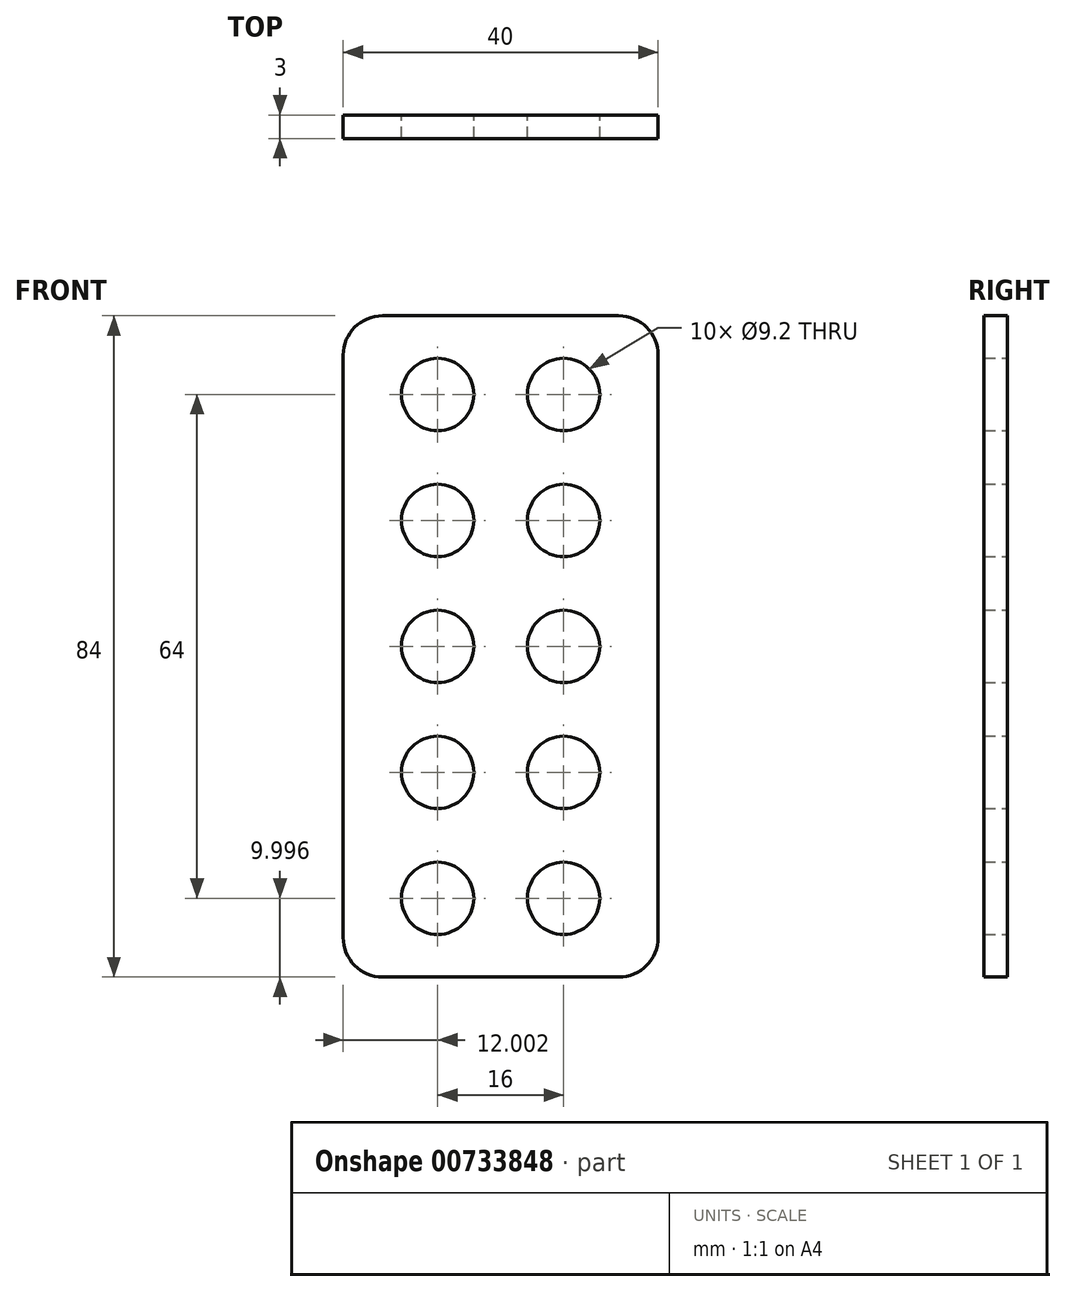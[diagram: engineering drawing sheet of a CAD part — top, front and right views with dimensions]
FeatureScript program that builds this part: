
annotation { "Feature Type Name" : "Feature", "Feature Type Description" : "" }
export const myFeature = defineFeature(function(context is Context, id is Id, definition is map)
    precondition{}
    {
        {
            var Q0;
            Q0=qCreatedBy(makeId("Front.planeOp"),FACE);
            var sketch = newSketch(context, id + "F0", { "sketchPlane" : qUnion([Q0])});
            skLineSegment(sketch, "E0.bottom", {"start": v(-43.9, 44.63) * mm, "end": v(-23.9, 44.63) * mm});
            skLineSegment(sketch, "E0.top", {"start": v(-43.9, -39.37) * mm, "end": v(-23.9, -39.37) * mm});
            skLineSegment(sketch, "E0.left", {"start": v(-43.9, 44.63) * mm, "end": v(-43.9, -39.37) * mm});
            skLineSegment(sketch, "E0.right", {"start": v(-23.9, 44.63) * mm, "end": v(-23.9, -39.37) * mm});
            skCircle(sketch, "E1", {"center": v(-31.9, 34.63) * mm, "radius": 4.6 * mm});
            skCircle(sketch, "E2", {"center": v(-31.9, 18.63) * mm, "radius": 4.6 * mm});
            skCircle(sketch, "E3", {"center": v(-31.9, 2.63) * mm, "radius": 4.6 * mm});
            skCircle(sketch, "E4", {"center": v(-31.9, -13.37) * mm, "radius": 4.6 * mm});
            skCircle(sketch, "E5", {"center": v(-31.9, -29.37) * mm, "radius": 4.6 * mm});
            skCircle(sketch, "E6.MirrorC", {"center": v(-15.9, -29.37) * mm, "radius": 4.6 * mm});
            skCircle(sketch, "E7.MirrorC", {"center": v(-15.9, -13.37) * mm, "radius": 4.6 * mm});
            skCircle(sketch, "E8.MirrorC", {"center": v(-15.9, 2.63) * mm, "radius": 4.6 * mm});
            skCircle(sketch, "E9.MirrorC", {"center": v(-15.9, 18.63) * mm, "radius": 4.6 * mm});
            skCircle(sketch, "E10.MirrorC", {"center": v(-15.9, 34.63) * mm, "radius": 4.6 * mm});
            skLineSegment(sketch, "E11.MirrorCS", {"start": v(-3.9, 44.63) * mm, "end": v(-3.9, -39.37) * mm});
            skLineSegment(sketch, "E12.MirrorCS", {"start": v(-3.9, 44.63) * mm, "end": v(-23.9, 44.63) * mm});
            skLineSegment(sketch, "E13.MirrorCS", {"start": v(-3.9, -39.37) * mm, "end": v(-23.9, -39.37) * mm});
            skSolve(sketch);
        }
        {
            var Q0;
            Q0 = qSketchRegion(id + "F0", true);
            extrude(context, id + "F1", {"entities" : qUnion([Q0]), "depth" : 3 * mm, "offsetDistance" : 25 * mm});
        }
        {
            var Q0;
            Q0=makeQuery(id+"F1.opExtrude","SWEPT_EDGE",EDGE,{"disambiguationData":[OSD([sQuery(id+"F0.wireOp",EDGE,"E0.bottom"),sQuery(id+"F0.wireOp",EDGE,"E0.left")])]});
            var Q1;
            Q1=makeQuery(id+"F1.opExtrude","SWEPT_EDGE",EDGE,{"disambiguationData":[OSD([sQuery(id+"F0.wireOp",EDGE,"E11.MirrorCS"),sQuery(id+"F0.wireOp",EDGE,"E12.MirrorCS")])]});
            var Q2;
            Q2=makeQuery(id+"F1.opExtrude","SWEPT_EDGE",EDGE,{"disambiguationData":[OSD([sQuery(id+"F0.wireOp",EDGE,"E11.MirrorCS"),sQuery(id+"F0.wireOp",EDGE,"E13.MirrorCS")])]});
            var Q3;
            Q3=makeQuery(id+"F1.opExtrude","SWEPT_EDGE",EDGE,{"disambiguationData":[OSD([sQuery(id+"F0.wireOp",EDGE,"E0.top"),sQuery(id+"F0.wireOp",EDGE,"E0.left")])]});
            fillet(context, id + "F2", {"entities" : qUnion([Q0, Q1, Q2, Q3]), "radius" : 5 * mm, "tangentPropagation" : true, "allowEdgeOverflow" : false});
        }
    });
